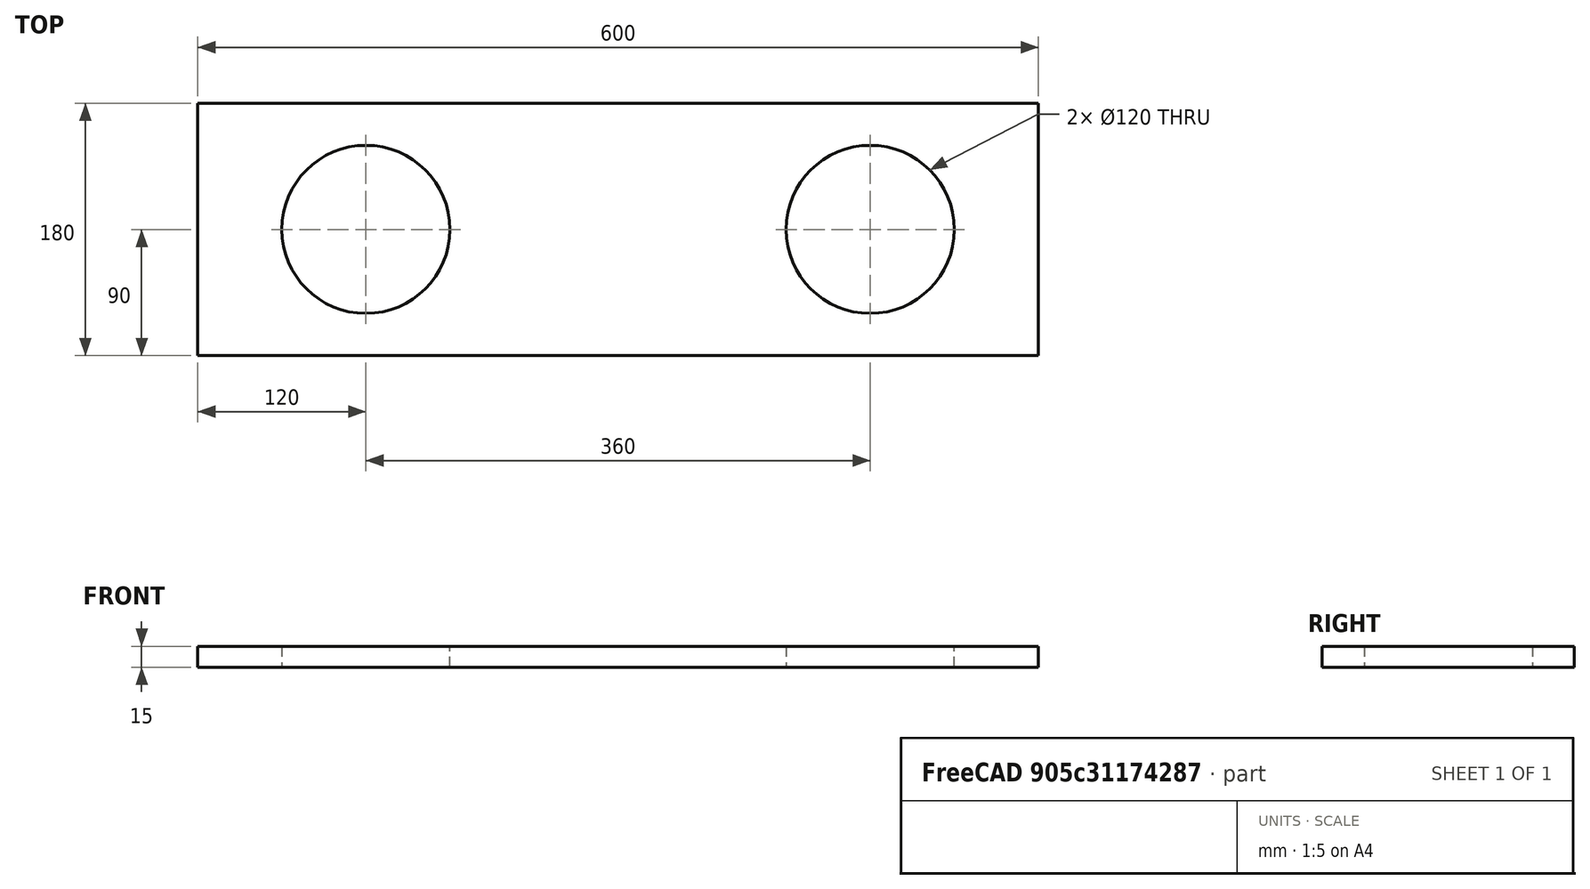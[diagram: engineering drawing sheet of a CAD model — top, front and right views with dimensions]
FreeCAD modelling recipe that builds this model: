
FCSTD DOCUMENT  (FreeCAD 1.0R39319 (Git))
Label: fan_plane
License: All rights reserved
LicenseURL: http://en.wikipedia.org/wiki/All_rights_reserved
objects: Sketcher::SketchObject×1, PartDesign::Pad×1, PartDesign::Body×1
note: 6 computed .brp shape members not serialized (recipe doc carries the construction recipe); baked Part::Feature solids carry a one-line shape summary decoded from their .brp

FEATURE [Sketcher::SketchObject] Sketch  label="fan_plane_sketch"
  ArcFitTolerance = 0
  AttachmentSupport = -> [XY_Plane]
  FullyConstrained = true
  MakeInternals = false
  MapMode = 5
  sketch-geometry (10):
    g0: LineSegment StartX=0 StartY=0 StartZ=0 EndX=600 EndY=0 EndZ=0
    g1: LineSegment StartX=600 StartY=0 StartZ=0 EndX=600 EndY=180 EndZ=0
    g2: LineSegment StartX=600 StartY=180 StartZ=0 EndX=0 EndY=180 EndZ=0
    g3: LineSegment StartX=0 StartY=180 StartZ=0 EndX=0 EndY=0 EndZ=0
    g4: Circle CenterX=120 CenterY=90 CenterZ=0 NormalX=0 NormalY=0 NormalZ=1 AngleXU=0 Radius=60
    g5: Circle CenterX=480 CenterY=90 CenterZ=0 NormalX=0 NormalY=0 NormalZ=1 AngleXU=0 Radius=60
    g6: LineSegment [constr] StartX=120 StartY=90 StartZ=0 EndX=0 EndY=90 EndZ=0
    g7: LineSegment [constr] StartX=480 StartY=90 StartZ=0 EndX=600 EndY=90 EndZ=0
    g8: LineSegment [constr] StartX=480 StartY=90 StartZ=0 EndX=480 EndY=0 EndZ=0
    g9: LineSegment [constr] StartX=120 StartY=90 StartZ=0 EndX=120 EndY=180 EndZ=0
  constraints (29):
    c: Coincident(g0,g1)
    c: Coincident(g1,g2)
    c: Coincident(g2,g3)
    c: Coincident(g3,g0)
    c: Horizontal(g0)
    c: Horizontal(g2)
    c: Vertical(g1)
    c: Vertical(g3)
    c: Coincident(g0,g-1)
    c: DistanceX(g0,g0) = 600
    c: DistanceY(g3,g3) = 180
    c: Radius(g4) = 60
    c: Radius(g5) = 60
    c: Coincident(g6,g4)
    c: PointOnObject(g6,g3)
    c: Horizontal(g6)
    c: Coincident(g7,g5)
    c: PointOnObject(g7,g1)
    c: Horizontal(g7)
    c: Coincident(g8,g5)
    c: PointOnObject(g8,g0)
    c: Vertical(g8)
    c: Equal(g6,g7)
    c: Coincident(g9,g4)
    c: PointOnObject(g9,g2)
    c: Vertical(g9)
    c: Equal(g9,g8)
    c: DistanceX(g6,g6) = 120
    c: PointOnObject(g4,g7)
FEATURE [PartDesign::Pad] Pad  label="fan_plane_pad"
  AllowMultiFace = false
  Direction = (0,0,1)
  Length = 15
  Length2 = 100
  Profile = -> Sketch
  ReferenceAxis = -> Sketch [N_Axis]
  Suppressed = false
  Type = 0
FEATURE [PartDesign::Body] Body  label="fan_plane_body"
  AllowCompound = false
  Group = -> [Sketch,Pad]
  Origin = -> Origin
  Tip = -> Pad
